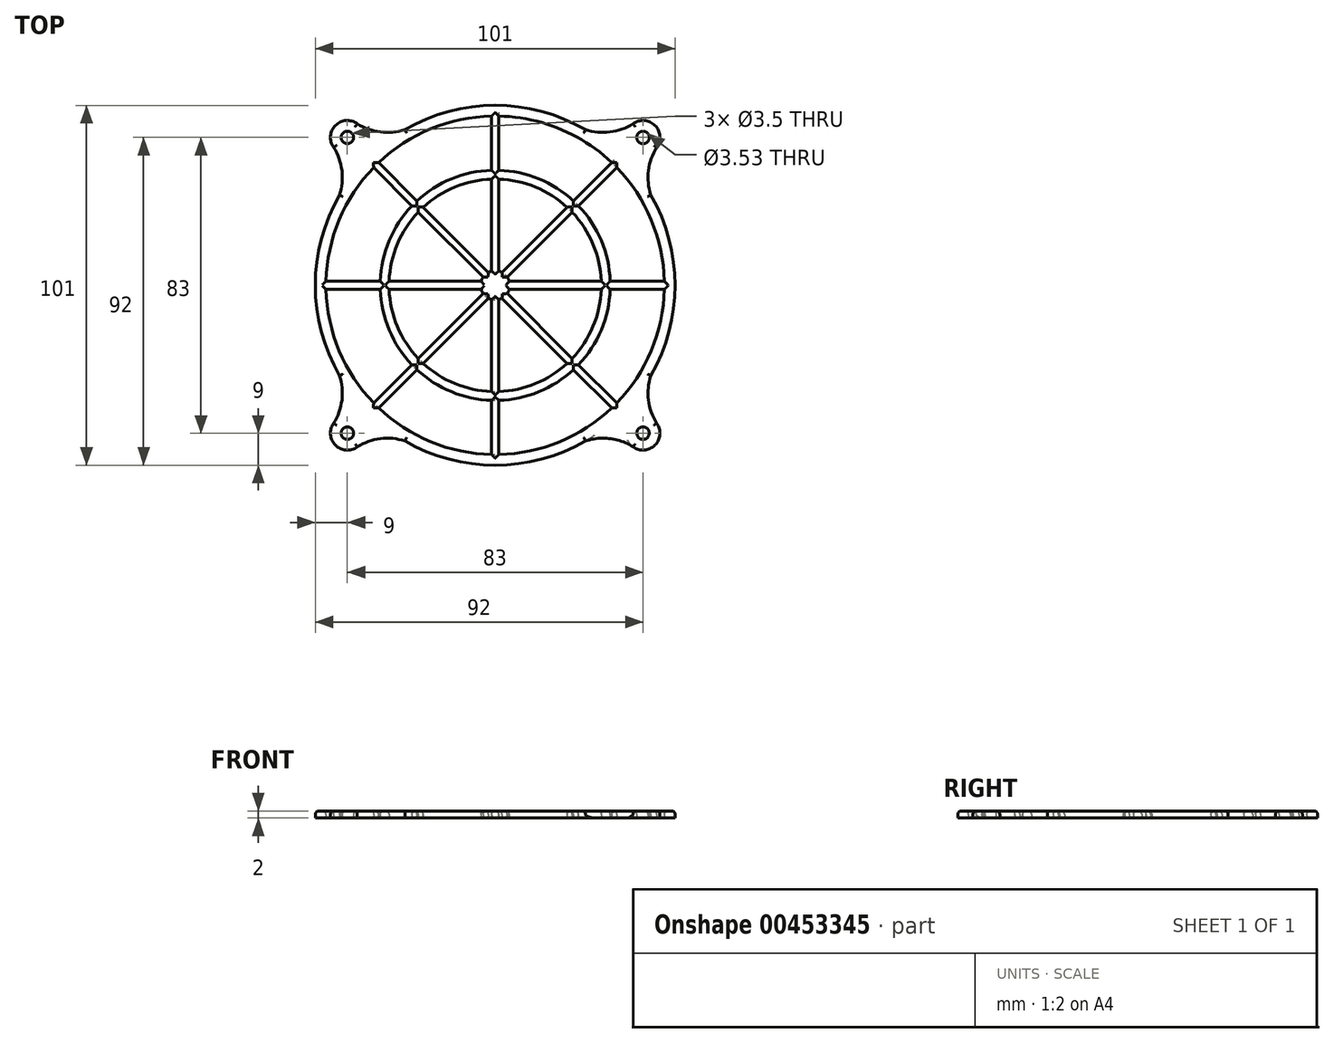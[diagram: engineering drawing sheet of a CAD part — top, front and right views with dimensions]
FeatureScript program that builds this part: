
annotation { "Feature Type Name" : "Feature", "Feature Type Description" : "" }
export const myFeature = defineFeature(function(context is Context, id is Id, definition is map)
    precondition{}
    {
        {
            var Q0;
            Q0=qCreatedBy(makeId("Top.planeOp"),FACE);
            var sketch = newSketch(context, id + "F0", { "sketchPlane" : qUnion([Q0])});
            skCircle(sketch, "E0", {"center": v(0, 0) * mm, "radius": 47.5 * mm});
            skCircle(sketch, "E1.0", {"center": v(0, 0) * mm, "radius": 50.5 * mm});
            skLineSegment(sketch, "E2", {"start": v(-74.72, 0) * mm, "end": v(73.28, 0) * mm, "construction": true});
            skLineSegment(sketch, "E3", {"start": v(0, 74.83) * mm, "end": v(0, -67.6) * mm, "construction": true});
            skCircle(sketch, "E4", {"center": v(0, 0) * mm, "radius": 4.1 * mm});
            skLineSegment(sketch, "E5", {"start": v(-1, 47.49) * mm, "end": v(-1, 3.98) * mm});
            skLineSegment(sketch, "E6", {"start": v(-47.49, 1.16) * mm, "end": v(-3.94, 1.16) * mm});
            skLineSegment(sketch, "E7", {"start": v(-1.9, 3.64) * mm, "end": v(-32.7, 34.44) * mm});
            skLineSegment(sketch, "E8", {"start": v(-34.13, 33.04) * mm, "end": v(-3.4, 2.3) * mm});
            skLineSegment(sketch, "E9.MirrorCS", {"start": v(-47.49, -1.16) * mm, "end": v(-3.94, -1.16) * mm});
            skLineSegment(sketch, "E10.MirrorCS", {"start": v(-34.13, -33.04) * mm, "end": v(-3.4, -2.3) * mm});
            skLineSegment(sketch, "E11.MirrorCS", {"start": v(-1.9, -3.64) * mm, "end": v(-32.7, -34.44) * mm});
            skLineSegment(sketch, "E12.MirrorCS", {"start": v(-1, -47.49) * mm, "end": v(-1, -3.98) * mm});
            skLineSegment(sketch, "E13.MirrorCS", {"start": v(1, 47.49) * mm, "end": v(1, 3.98) * mm});
            skLineSegment(sketch, "E14.MirrorCS", {"start": v(1.9, 3.64) * mm, "end": v(32.7, 34.44) * mm});
            skLineSegment(sketch, "E15.MirrorCS", {"start": v(34.13, 33.04) * mm, "end": v(3.4, 2.3) * mm});
            skLineSegment(sketch, "E16.MirrorCS", {"start": v(47.49, 1.16) * mm, "end": v(3.94, 1.16) * mm});
            skLineSegment(sketch, "E17.MirrorCS", {"start": v(34.13, -33.04) * mm, "end": v(3.4, -2.3) * mm});
            skLineSegment(sketch, "E18.MirrorCS", {"start": v(1, -47.49) * mm, "end": v(1, -3.98) * mm});
            skLineSegment(sketch, "E19.MirrorCS", {"start": v(1.9, -3.64) * mm, "end": v(32.7, -34.44) * mm});
            skLineSegment(sketch, "E20.MirrorCS", {"start": v(47.49, -1.16) * mm, "end": v(3.94, -1.16) * mm});
            skLineSegment(sketch, "E21.bottom", {"start": v(41.5, 41.5) * mm, "end": v(-41.5, 41.5) * mm, "construction": true});
            skLineSegment(sketch, "E21.top", {"start": v(41.5, -41.5) * mm, "end": v(-41.5, -41.5) * mm, "construction": true});
            skLineSegment(sketch, "E21.left", {"start": v(41.5, 41.5) * mm, "end": v(41.5, -41.5) * mm, "construction": true});
            skLineSegment(sketch, "E21.right", {"start": v(-41.5, 41.5) * mm, "end": v(-41.5, -41.5) * mm, "construction": true});
            skCircle(sketch, "E22", {"center": v(41.5, 41.5) * mm, "radius": 1.77 * mm});
            skCircle(sketch, "E23", {"center": v(-41.5, 41.5) * mm, "radius": 1.75 * mm});
            skCircle(sketch, "E24", {"center": v(-41.5, -41.5) * mm, "radius": 1.75 * mm});
            skCircle(sketch, "E25", {"center": v(41.5, -41.5) * mm, "radius": 1.75 * mm});
            skCircle(sketch, "E26.0", {"center": v(-41.5, 41.5) * mm, "radius": 4.75 * mm});
            skArc(sketch, "E27", {"start": v(-43.69, 25.33) * mm, "mid": v(-43.05, 32.44) * mm, "end": v(-45.6, 39.1) * mm});
            skLineSegment(sketch, "E28", {"start": v(-41.5, 41.5) * mm, "end": v(41.5, -41.5) * mm, "construction": true});
            skArc(sketch, "E29.MirrorCS", {"start": v(-25.33, 43.69) * mm, "mid": v(-32.44, 43.05) * mm, "end": v(-39.1, 45.6) * mm});
            skArc(sketch, "E30.MirrorCS", {"start": v(25.33, 43.69) * mm, "mid": v(32.44, 43.05) * mm, "end": v(39.1, 45.6) * mm});
            skArc(sketch, "E31.MirrorCS", {"start": v(43.69, 25.33) * mm, "mid": v(43.05, 32.44) * mm, "end": v(45.6, 39.1) * mm});
            skCircle(sketch, "E32.MirrorC", {"center": v(41.5, 41.5) * mm, "radius": 4.75 * mm});
            skArc(sketch, "E33.MirrorCS", {"start": v(-43.69, -25.33) * mm, "mid": v(-43.05, -32.44) * mm, "end": v(-45.6, -39.1) * mm});
            skCircle(sketch, "E34.MirrorC", {"center": v(-41.5, -41.5) * mm, "radius": 4.75 * mm});
            skArc(sketch, "E35.MirrorCS", {"start": v(-25.33, -43.69) * mm, "mid": v(-32.44, -43.05) * mm, "end": v(-39.1, -45.6) * mm});
            skArc(sketch, "E36.MirrorCS", {"start": v(25.33, -43.69) * mm, "mid": v(32.44, -43.05) * mm, "end": v(39.1, -45.6) * mm});
            skCircle(sketch, "E37.MirrorC", {"center": v(41.5, -41.5) * mm, "radius": 4.75 * mm});
            skArc(sketch, "E38.MirrorCS", {"start": v(43.69, -25.33) * mm, "mid": v(43.05, -32.44) * mm, "end": v(45.6, -39.1) * mm});
            skCircle(sketch, "E39", {"center": v(0, 0) * mm, "radius": 32.3 * mm});
            skCircle(sketch, "E40", {"center": v(0, 0) * mm, "radius": 29.8 * mm});
            skSolve(sketch);
        }
        {
            var Q0;
            Q0 = qSketchRegion(id + "F0", true);
            var Q1;
            {var subQ0=sQuery(id+"F0.wireOp",EDGE,"E6");Q1=makeQuery(id+"F0.imprint","IMPRINT",FACE,{"disambiguationData":[TD([[makeQuery(id+"F0.imprint","IMPRINT",EDGE,{"derivedFrom":subQ0}),-1.0]])]});}
            var Q2;
            {var subQ0=sQuery(id+"F0.wireOp",EDGE,"E7");Q2=makeQuery(id+"F0.imprint","IMPRINT",FACE,{"disambiguationData":[TD([[makeQuery(id+"F0.imprint","IMPRINT",EDGE,{"derivedFrom":subQ0}),1.0]])]});}
            var Q3;
            {var subQ0=sQuery(id+"F0.wireOp",EDGE,"E5");Q3=makeQuery(id+"F0.imprint","IMPRINT",FACE,{"disambiguationData":[TD([[makeQuery(id+"F0.imprint","IMPRINT",EDGE,{"derivedFrom":subQ0}),1.0]])]});}
            var Q4;
            {var subQ0=sQuery(id+"F0.wireOp",EDGE,"E14.MirrorCS");Q4=makeQuery(id+"F0.imprint","IMPRINT",FACE,{"disambiguationData":[TD([[makeQuery(id+"F0.imprint","IMPRINT",EDGE,{"derivedFrom":subQ0}),-1.0]])]});}
            var Q5;
            {var subQ0=sQuery(id+"F0.wireOp",EDGE,"E19.MirrorCS");Q5=makeQuery(id+"F0.imprint","IMPRINT",FACE,{"disambiguationData":[TD([[makeQuery(id+"F0.imprint","IMPRINT",EDGE,{"derivedFrom":subQ0}),1.0]])]});}
            var Q6;
            {var subQ0=sQuery(id+"F0.wireOp",EDGE,"E12.MirrorCS");Q6=makeQuery(id+"F0.imprint","IMPRINT",FACE,{"disambiguationData":[TD([[makeQuery(id+"F0.imprint","IMPRINT",EDGE,{"derivedFrom":subQ0}),-1.0]])]});}
            var Q7;
            {var subQ0=sQuery(id+"F0.wireOp",EDGE,"E10.MirrorCS");Q7=makeQuery(id+"F0.imprint","IMPRINT",FACE,{"disambiguationData":[TD([[makeQuery(id+"F0.imprint","IMPRINT",EDGE,{"derivedFrom":subQ0}),-1.0]])]});}
            var Q8;
            {var subQ0=sQuery(id+"F0.wireOp",EDGE,"E16.MirrorCS");Q8=makeQuery(id+"F0.imprint","IMPRINT",FACE,{"disambiguationData":[TD([[makeQuery(id+"F0.imprint","IMPRINT",EDGE,{"derivedFrom":subQ0}),1.0]])]});}
            var Q9;
            {var subQ0=sQuery(id+"F0.wireOp",EDGE,"E4");var subQ8=makeQuery(id+"F0.imprint","INTERSECT",VERTEX,{"derivedFrom":[subQ0,sQuery(id+"F0.wireOp",EDGE,"E15.MirrorCS")]});Q9=makeQuery(id+"F0.imprint","IMPRINT",FACE,{"disambiguationData":[TD([[makeQuery(id+"F0.imprint","IMPRINT",EDGE,{"disambiguationData":[TD([[subQ8,1.0]])],"derivedFrom":subQ0}),1.0]])]});}
            var Q10;
            {var subQ0=sQuery(id+"F0.wireOp",EDGE,"E39");var subQ1=sQuery(id+"F0.wireOp",EDGE,"E6");var subQ2=makeQuery(id+"F0.imprint","INTERSECT",VERTEX,{"derivedFrom":[subQ1,subQ0]});Q10=makeQuery(id+"F0.imprint","IMPRINT",FACE,{"disambiguationData":[TD([[makeQuery(id+"F0.imprint","IMPRINT",EDGE,{"disambiguationData":[TD([[subQ2,-1.0]])],"derivedFrom":subQ1}),1.0]])]});}
            var Q11;
            {var subQ0=sQuery(id+"F0.wireOp",EDGE,"E40");var subQ1=sQuery(id+"F0.wireOp",EDGE,"E11.MirrorCS");var subQ2=makeQuery(id+"F0.imprint","INTERSECT",VERTEX,{"derivedFrom":[subQ1,subQ0]});Q11=makeQuery(id+"F0.imprint","IMPRINT",FACE,{"disambiguationData":[TD([[makeQuery(id+"F0.imprint","IMPRINT",EDGE,{"disambiguationData":[TD([[subQ2,-1.0]])],"derivedFrom":subQ1}),1.0]])]});}
            var Q12;
            {var subQ0=sQuery(id+"F0.wireOp",EDGE,"E39");var subQ1=sQuery(id+"F0.wireOp",EDGE,"E18.MirrorCS");var subQ2=makeQuery(id+"F0.imprint","INTERSECT",VERTEX,{"derivedFrom":[subQ1,subQ0]});Q12=makeQuery(id+"F0.imprint","IMPRINT",FACE,{"disambiguationData":[TD([[makeQuery(id+"F0.imprint","IMPRINT",EDGE,{"disambiguationData":[TD([[subQ2,-1.0]])],"derivedFrom":subQ1}),-1.0]])]});}
            var Q13;
            {var subQ0=sQuery(id+"F0.wireOp",EDGE,"E39");var subQ1=sQuery(id+"F0.wireOp",EDGE,"E17.MirrorCS");var subQ2=makeQuery(id+"F0.imprint","INTERSECT",VERTEX,{"derivedFrom":[subQ1,subQ0]});Q13=makeQuery(id+"F0.imprint","IMPRINT",FACE,{"disambiguationData":[TD([[makeQuery(id+"F0.imprint","IMPRINT",EDGE,{"disambiguationData":[TD([[subQ2,-1.0]])],"derivedFrom":subQ1}),-1.0]])]});}
            var Q14;
            {var subQ0=sQuery(id+"F0.wireOp",EDGE,"E39");var subQ1=sQuery(id+"F0.wireOp",EDGE,"E15.MirrorCS");var subQ2=makeQuery(id+"F0.imprint","INTERSECT",VERTEX,{"derivedFrom":[subQ1,subQ0]});Q14=makeQuery(id+"F0.imprint","IMPRINT",FACE,{"disambiguationData":[TD([[makeQuery(id+"F0.imprint","IMPRINT",EDGE,{"disambiguationData":[TD([[subQ2,-1.0]])],"derivedFrom":subQ1}),1.0]])]});}
            var Q15;
            {var subQ0=sQuery(id+"F0.wireOp",EDGE,"E39");var subQ1=sQuery(id+"F0.wireOp",EDGE,"E13.MirrorCS");var subQ2=makeQuery(id+"F0.imprint","INTERSECT",VERTEX,{"derivedFrom":[subQ1,subQ0]});Q15=makeQuery(id+"F0.imprint","IMPRINT",FACE,{"disambiguationData":[TD([[makeQuery(id+"F0.imprint","IMPRINT",EDGE,{"disambiguationData":[TD([[subQ2,-1.0]])],"derivedFrom":subQ1}),1.0]])]});}
            var Q16;
            {var subQ0=sQuery(id+"F0.wireOp",EDGE,"E39");var subQ1=sQuery(id+"F0.wireOp",EDGE,"E9.MirrorCS");var subQ2=makeQuery(id+"F0.imprint","INTERSECT",VERTEX,{"derivedFrom":[subQ1,subQ0]});Q16=makeQuery(id+"F0.imprint","IMPRINT",FACE,{"disambiguationData":[TD([[makeQuery(id+"F0.imprint","IMPRINT",EDGE,{"disambiguationData":[TD([[subQ2,-1.0]])],"derivedFrom":subQ1}),-1.0]])]});}
            var Q17;
            {var subQ0=sQuery(id+"F0.wireOp",EDGE,"E39");var subQ1=sQuery(id+"F0.wireOp",EDGE,"E5");var subQ2=makeQuery(id+"F0.imprint","INTERSECT",VERTEX,{"derivedFrom":[subQ1,subQ0]});Q17=makeQuery(id+"F0.imprint","IMPRINT",FACE,{"disambiguationData":[TD([[makeQuery(id+"F0.imprint","IMPRINT",EDGE,{"disambiguationData":[TD([[subQ2,-1.0]])],"derivedFrom":subQ1}),-1.0]])]});}
            extrude(context, id + "F1", {"entities" : qUnion([Q0, Q1, Q2, Q3, Q4, Q5, Q6, Q7, Q8, Q9, Q10, Q11, Q12, Q13, Q14, Q15, Q16, Q17]), "depth" : 2 * mm});
        }
        {
            var Q0;
            {var subQ0=sQuery(id+"F0.wireOp",EDGE,"E0");Q0=makeQuery(id+"F1.opExtrude","CAP_EDGE",EDGE,{"disambiguationData":[OSD([subQ0]),TDD([makeQuery(id+"F0.imprint","IMPRINT",EDGE,{"disambiguationData":[TD([[makeQuery(id+"F0.imprint","INTERSECT",VERTEX,{"derivedFrom":[subQ0,sQuery(id+"F0.wireOp",EDGE,"E6")]}),1.0]])],"derivedFrom":subQ0})])],"isStart":false});}
            var Q1;
            Q1=makeQuery(id+"F1.opExtrude","CAP_EDGE",EDGE,{"disambiguationData":[OSD([sQuery(id+"F0.wireOp",EDGE,"E8")])],"isStart":false});
            var Q2;
            {var subQ0=sQuery(id+"F0.wireOp",EDGE,"E0");Q2=makeQuery(id+"F1.opExtrude","CAP_EDGE",EDGE,{"disambiguationData":[OSD([subQ0]),TDD([makeQuery(id+"F0.imprint","IMPRINT",EDGE,{"disambiguationData":[TD([[makeQuery(id+"F0.imprint","INTERSECT",VERTEX,{"derivedFrom":[subQ0,sQuery(id+"F0.wireOp",EDGE,"E5")]}),-1.0]])],"derivedFrom":subQ0})])],"isStart":false});}
            var Q3;
            Q3=makeQuery(id+"F1.opExtrude","CAP_EDGE",EDGE,{"disambiguationData":[OSD([sQuery(id+"F0.wireOp",EDGE,"E5")])],"isStart":false});
            var Q4;
            Q4=makeQuery(id+"F1.opExtrude","CAP_EDGE",EDGE,{"disambiguationData":[OSD([sQuery(id+"F0.wireOp",EDGE,"E13.MirrorCS")])],"isStart":false});
            var Q5;
            {var subQ0=sQuery(id+"F0.wireOp",EDGE,"E0");Q5=makeQuery(id+"F1.opExtrude","CAP_EDGE",EDGE,{"disambiguationData":[OSD([subQ0]),TDD([makeQuery(id+"F0.imprint","IMPRINT",EDGE,{"disambiguationData":[TD([[makeQuery(id+"F0.imprint","INTERSECT",VERTEX,{"derivedFrom":[subQ0,sQuery(id+"F0.wireOp",EDGE,"E13.MirrorCS")]}),1.0]])],"derivedFrom":subQ0})])],"isStart":true});}
            var Q6;
            Q6=makeQuery(id+"F1.opExtrude","CAP_EDGE",EDGE,{"disambiguationData":[OSD([sQuery(id+"F0.wireOp",EDGE,"E14.MirrorCS")])],"isStart":false});
            var Q7;
            Q7=makeQuery(id+"F1.opExtrude","CAP_EDGE",EDGE,{"disambiguationData":[OSD([sQuery(id+"F0.wireOp",EDGE,"E15.MirrorCS")])],"isStart":true});
            var Q8;
            {var subQ0=sQuery(id+"F0.wireOp",EDGE,"E0");Q8=makeQuery(id+"F1.opExtrude","CAP_EDGE",EDGE,{"disambiguationData":[OSD([subQ0]),TDD([makeQuery(id+"F0.imprint","IMPRINT",EDGE,{"disambiguationData":[TD([[makeQuery(id+"F0.imprint","INTERSECT",VERTEX,{"derivedFrom":[subQ0,sQuery(id+"F0.wireOp",EDGE,"E15.MirrorCS")]}),1.0]])],"derivedFrom":subQ0})])],"isStart":false});}
            var Q9;
            Q9=makeQuery(id+"F1.opExtrude","CAP_EDGE",EDGE,{"disambiguationData":[OSD([sQuery(id+"F0.wireOp",EDGE,"E16.MirrorCS")])],"isStart":false});
            var Q10;
            Q10=makeQuery(id+"F1.opExtrude","CAP_EDGE",EDGE,{"disambiguationData":[OSD([sQuery(id+"F0.wireOp",EDGE,"E20.MirrorCS")])],"isStart":false});
            var Q11;
            {var subQ0=sQuery(id+"F0.wireOp",EDGE,"E0");Q11=makeQuery(id+"F1.opExtrude","CAP_EDGE",EDGE,{"disambiguationData":[OSD([subQ0]),TDD([makeQuery(id+"F0.imprint","IMPRINT",EDGE,{"disambiguationData":[TD([[makeQuery(id+"F0.imprint","INTERSECT",VERTEX,{"derivedFrom":[subQ0,sQuery(id+"F0.wireOp",EDGE,"E17.MirrorCS")]}),-1.0]])],"derivedFrom":subQ0})])],"isStart":false});}
            var Q12;
            Q12=makeQuery(id+"F1.opExtrude","CAP_EDGE",EDGE,{"disambiguationData":[OSD([sQuery(id+"F0.wireOp",EDGE,"E17.MirrorCS")])],"isStart":false});
            var Q13;
            Q13=makeQuery(id+"F1.opExtrude","CAP_EDGE",EDGE,{"disambiguationData":[OSD([sQuery(id+"F0.wireOp",EDGE,"E19.MirrorCS")])],"isStart":false});
            var Q14;
            Q14=makeQuery(id+"F1.opExtrude","CAP_EDGE",EDGE,{"disambiguationData":[OSD([sQuery(id+"F0.wireOp",EDGE,"E18.MirrorCS")])],"isStart":false});
            var Q15;
            Q15=makeQuery(id+"F1.opExtrude","CAP_EDGE",EDGE,{"disambiguationData":[OSD([sQuery(id+"F0.wireOp",EDGE,"E12.MirrorCS")])],"isStart":true});
            var Q16;
            Q16=makeQuery(id+"F1.opExtrude","CAP_EDGE",EDGE,{"disambiguationData":[OSD([sQuery(id+"F0.wireOp",EDGE,"E11.MirrorCS")])],"isStart":true});
            var Q17;
            Q17=makeQuery(id+"F1.opExtrude","CAP_EDGE",EDGE,{"disambiguationData":[OSD([sQuery(id+"F0.wireOp",EDGE,"E10.MirrorCS")])],"isStart":false});
            var Q18;
            Q18=makeQuery(id+"F1.opExtrude","CAP_EDGE",EDGE,{"disambiguationData":[OSD([sQuery(id+"F0.wireOp",EDGE,"E9.MirrorCS")])],"isStart":false});
            var Q19;
            Q19=makeQuery(id+"F1.opExtrude","CAP_EDGE",EDGE,{"disambiguationData":[OSD([sQuery(id+"F0.wireOp",EDGE,"E6")])],"isStart":false});
            var Q20;
            {var subQ0=sQuery(id+"F0.wireOp",EDGE,"E0");Q20=makeQuery(id+"F1.opExtrude","CAP_EDGE",EDGE,{"disambiguationData":[OSD([subQ0]),TDD([makeQuery(id+"F0.imprint","IMPRINT",EDGE,{"disambiguationData":[TD([[makeQuery(id+"F0.imprint","INTERSECT",VERTEX,{"derivedFrom":[subQ0,sQuery(id+"F0.wireOp",EDGE,"E9.MirrorCS")]}),-1.0]])],"derivedFrom":subQ0})])],"isStart":false});}
            var Q21;
            {var subQ0=sQuery(id+"F0.wireOp",EDGE,"E0");Q21=makeQuery(id+"F1.opExtrude","CAP_EDGE",EDGE,{"disambiguationData":[OSD([subQ0]),TDD([makeQuery(id+"F0.imprint","IMPRINT",EDGE,{"disambiguationData":[TD([[makeQuery(id+"F0.imprint","INTERSECT",VERTEX,{"derivedFrom":[subQ0,sQuery(id+"F0.wireOp",EDGE,"E11.MirrorCS")]}),-1.0]])],"derivedFrom":subQ0})])],"isStart":false});}
            var Q22;
            {var subQ0=sQuery(id+"F0.wireOp",EDGE,"E1.0");Q22=makeQuery(id+"F1.opExtrude","CAP_EDGE",EDGE,{"disambiguationData":[OSD([subQ0]),TDD([makeQuery(id+"F0.imprint","IMPRINT",EDGE,{"disambiguationData":[TD([[makeQuery(id+"F0.imprint","INTERSECT",VERTEX,{"derivedFrom":[subQ0,sQuery(id+"F0.wireOp",EDGE,"E35.MirrorCS")]}),-1.0]])],"derivedFrom":subQ0})])],"isStart":false});}
            var Q23;
            Q23=makeQuery(id+"F1.opExtrude","CAP_EDGE",EDGE,{"disambiguationData":[OSD([sQuery(id+"F0.wireOp",EDGE,"E36.MirrorCS")])],"isStart":true});
            var Q24;
            Q24=makeQuery(id+"F1.opExtrude","CAP_EDGE",EDGE,{"disambiguationData":[OSD([sQuery(id+"F0.wireOp",EDGE,"E37.MirrorC")])],"isStart":false});
            var Q25;
            Q25=makeQuery(id+"F1.opExtrude","CAP_EDGE",EDGE,{"disambiguationData":[OSD([sQuery(id+"F0.wireOp",EDGE,"E38.MirrorCS")])],"isStart":false});
            var Q26;
            {var subQ0=sQuery(id+"F0.wireOp",EDGE,"E1.0");Q26=makeQuery(id+"F1.opExtrude","CAP_EDGE",EDGE,{"disambiguationData":[OSD([subQ0]),TDD([makeQuery(id+"F0.imprint","IMPRINT",EDGE,{"disambiguationData":[TD([[makeQuery(id+"F0.imprint","INTERSECT",VERTEX,{"derivedFrom":[subQ0,sQuery(id+"F0.wireOp",EDGE,"E31.MirrorCS")]}),1.0]])],"derivedFrom":subQ0})])],"isStart":false});}
            var Q27;
            Q27=makeQuery(id+"F1.opExtrude","CAP_EDGE",EDGE,{"disambiguationData":[OSD([sQuery(id+"F0.wireOp",EDGE,"E31.MirrorCS")])],"isStart":false});
            var Q28;
            Q28=makeQuery(id+"F1.opExtrude","CAP_EDGE",EDGE,{"disambiguationData":[OSD([sQuery(id+"F0.wireOp",EDGE,"E32.MirrorC")])],"isStart":false});
            var Q29;
            Q29=makeQuery(id+"F1.opExtrude","CAP_EDGE",EDGE,{"disambiguationData":[OSD([sQuery(id+"F0.wireOp",EDGE,"E30.MirrorCS")])],"isStart":false});
            var Q30;
            Q30=makeQuery(id+"F1.opExtrude","CAP_FACE",FACE,{"disambiguationData":[OSD([sQuery(id+"F0.wireOp",EDGE,"E0"),sQuery(id+"F0.wireOp",EDGE,"E1.0"),sQuery(id+"F0.wireOp",EDGE,"E4"),sQuery(id+"F0.wireOp",EDGE,"E5"),sQuery(id+"F0.wireOp",EDGE,"E6"),sQuery(id+"F0.wireOp",EDGE,"E7"),sQuery(id+"F0.wireOp",EDGE,"E8"),sQuery(id+"F0.wireOp",EDGE,"E9.MirrorCS"),sQuery(id+"F0.wireOp",EDGE,"E10.MirrorCS"),sQuery(id+"F0.wireOp",EDGE,"E11.MirrorCS"),sQuery(id+"F0.wireOp",EDGE,"E12.MirrorCS"),sQuery(id+"F0.wireOp",EDGE,"E13.MirrorCS"),sQuery(id+"F0.wireOp",EDGE,"E14.MirrorCS"),sQuery(id+"F0.wireOp",EDGE,"E15.MirrorCS"),sQuery(id+"F0.wireOp",EDGE,"E16.MirrorCS"),sQuery(id+"F0.wireOp",EDGE,"E18.MirrorCS"),sQuery(id+"F0.wireOp",EDGE,"E19.MirrorCS"),sQuery(id+"F0.wireOp",EDGE,"E17.MirrorCS"),sQuery(id+"F0.wireOp",EDGE,"E20.MirrorCS"),sQuery(id+"F0.wireOp",EDGE,"E22"),sQuery(id+"F0.wireOp",EDGE,"E23"),sQuery(id+"F0.wireOp",EDGE,"E24"),sQuery(id+"F0.wireOp",EDGE,"E25"),sQuery(id+"F0.wireOp",EDGE,"E26.0"),sQuery(id+"F0.wireOp",EDGE,"E27"),sQuery(id+"F0.wireOp",EDGE,"E29.MirrorCS"),sQuery(id+"F0.wireOp",EDGE,"E30.MirrorCS"),sQuery(id+"F0.wireOp",EDGE,"E31.MirrorCS"),sQuery(id+"F0.wireOp",EDGE,"E32.MirrorC"),sQuery(id+"F0.wireOp",EDGE,"E33.MirrorCS"),sQuery(id+"F0.wireOp",EDGE,"E34.MirrorC"),sQuery(id+"F0.wireOp",EDGE,"E35.MirrorCS"),sQuery(id+"F0.wireOp",EDGE,"E36.MirrorCS"),sQuery(id+"F0.wireOp",EDGE,"E37.MirrorC"),sQuery(id+"F0.wireOp",EDGE,"E38.MirrorCS")])],"isStart":false});
            fillet(context, id + "F2", {"entities" : qUnion([Q0, Q1, Q2, Q3, Q4, Q5, Q6, Q7, Q8, Q9, Q10, Q11, Q12, Q13, Q14, Q15, Q16, Q17, Q18, Q19, Q20, Q21, Q22, Q23, Q24, Q25, Q26, Q27, Q28, Q29, Q30]), "radius" : 1 * mm, "tangentPropagation" : true, "allowEdgeOverflow" : false});
        }
    });
